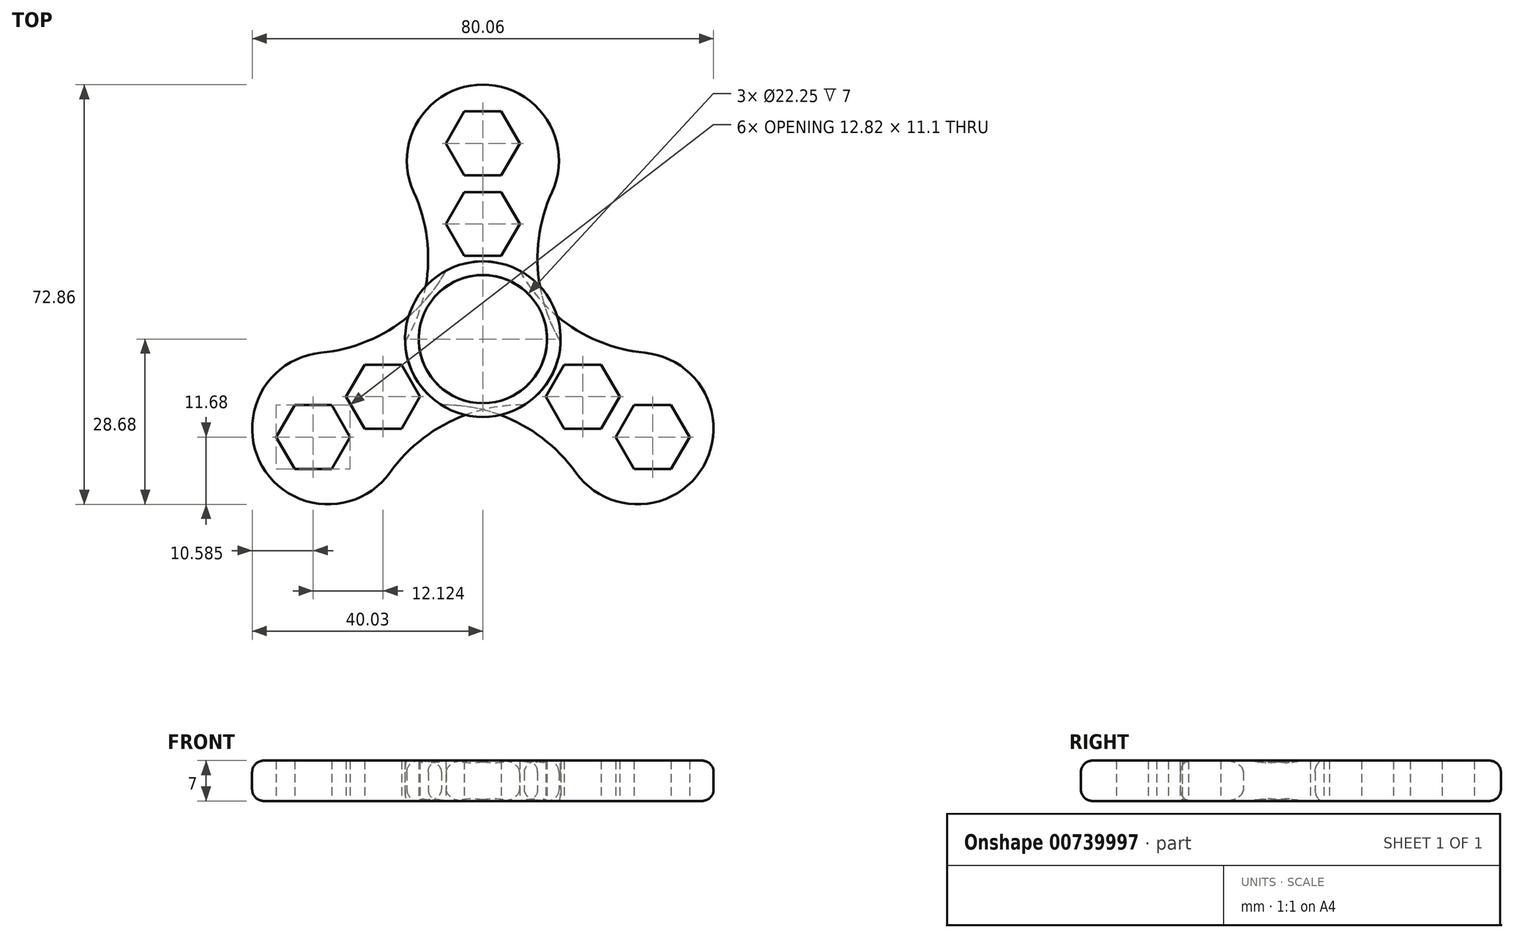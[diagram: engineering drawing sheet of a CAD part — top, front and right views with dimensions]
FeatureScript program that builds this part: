
annotation { "Feature Type Name" : "Feature", "Feature Type Description" : "" }
export const myFeature = defineFeature(function(context is Context, id is Id, definition is map)
    precondition{}
    {
        {
            var Q0;
            Q0=qCreatedBy(makeId("Top.planeOp"),FACE);
            var sketch = newSketch(context, id + "F0", { "sketchPlane" : qUnion([Q0])});
            skCircle(sketch, "E0", {"center": v(0, 0) * mm, "radius": 11.12 * mm});
            skCircle(sketch, "E1.cCircle", {"center": v(0, 20) * mm, "radius": 5.55 * mm, "construction": true});
            skLineSegment(sketch, "E1.0", {"start": v(3.2, 14.45) * mm, "end": v(-3.2, 14.45) * mm});
            skLineSegment(sketch, "E1.1", {"start": v(-3.2, 14.45) * mm, "end": v(-6.4, 20) * mm});
            skLineSegment(sketch, "E1.2", {"start": v(-6.4, 20) * mm, "end": v(-3.2, 25.55) * mm});
            skLineSegment(sketch, "E1.3", {"start": v(-3.2, 25.55) * mm, "end": v(3.2, 25.55) * mm});
            skLineSegment(sketch, "E1.4", {"start": v(3.2, 25.55) * mm, "end": v(6.4, 20) * mm});
            skLineSegment(sketch, "E1.5", {"start": v(6.4, 20) * mm, "end": v(3.2, 14.45) * mm});
            skPoint(sketch, "E1.0.midPoint", {"position": v(0, 14.45) * mm});
            skArc(sketch, "E2", {"start": v(-13.5, -0.48) * mm, "mid": v(0, -13.5) * mm, "end": v(13.5, -0.48) * mm});
            skArc(sketch, "E3", {"start": v(-6.64, 19.6) * mm, "mid": v(-6.05, 19.29) * mm, "end": v(-5.46, 19) * mm});
            skArc(sketch, "E4", {"start": v(-13.5, -0.48) * mm, "mid": v(-9.53, 12.35) * mm, "end": v(-12, 25.54) * mm});
            skArc(sketch, "E5", {"start": v(12, 25.54) * mm, "mid": v(9.53, 12.35) * mm, "end": v(13.5, -0.48) * mm});
            skPoint(sketch, "E6", {"position": v(0, 25.55) * mm});
            skCircle(sketch, "E7.cCircle", {"center": v(0, 34) * mm, "radius": 5.55 * mm, "construction": true});
            skLineSegment(sketch, "E7.0", {"start": v(3.2, 28.45) * mm, "end": v(-3.2, 28.45) * mm});
            skLineSegment(sketch, "E7.1", {"start": v(-3.2, 28.45) * mm, "end": v(-6.4, 34) * mm});
            skLineSegment(sketch, "E7.2", {"start": v(-6.4, 34) * mm, "end": v(-3.2, 39.55) * mm});
            skLineSegment(sketch, "E7.3", {"start": v(-3.2, 39.55) * mm, "end": v(3.2, 39.55) * mm});
            skLineSegment(sketch, "E7.4", {"start": v(3.2, 39.55) * mm, "end": v(6.4, 34) * mm});
            skLineSegment(sketch, "E7.5", {"start": v(6.4, 34) * mm, "end": v(3.2, 28.45) * mm});
            skPoint(sketch, "E7.0.midPoint", {"position": v(0, 28.45) * mm});
            skArc(sketch, "E8.trimOffspring", {"start": v(5.46, 19) * mm, "mid": v(6.05, 19.29) * mm, "end": v(6.64, 19.6) * mm});
            skArc(sketch, "E9.trimOffspring", {"start": v(12, 25.54) * mm, "mid": v(0, 44.18) * mm, "end": v(-12, 25.54) * mm});
            skSolve(sketch);
        }
        {
            var Q0;
            Q0=makeQuery(id+"F0.imprint","IMPRINT",FACE,{"disambiguationData":[TD([[makeQuery(id+"F0.imprint","IMPRINT",EDGE,{"derivedFrom":sQuery(id+"F0.wireOp",EDGE,"E0")}),-1.0]])]});
            extrude(context, id + "F1", {"entities" : qUnion([Q0]), "depth" : 7 * mm, "offsetDistance" : 25 * mm});
        }
        {
            var Q0;
            Q0=makeQuery(id+"F1.opExtrude","SWEPT_BODY",BODY,{"disambiguationData":[OSD([sQuery(id+"F0.wireOp",EDGE,"E0"),sQuery(id+"F0.wireOp",EDGE,"MDsEToRO-sDo8-RBbG-tWF8-SreFTiSiscwj"),sQuery(id+"F0.wireOp",EDGE,"8695b1e1-9288-4cb8-b92b-e351c22f4dc8.0"),sQuery(id+"F0.wireOp",EDGE,"8695b1e1-9288-4cb8-b92b-e351c22f4dc8.1"),sQuery(id+"F0.wireOp",EDGE,"8695b1e1-9288-4cb8-b92b-e351c22f4dc8.2"),sQuery(id+"F0.wireOp",EDGE,"8695b1e1-9288-4cb8-b92b-e351c22f4dc8.3"),sQuery(id+"F0.wireOp",EDGE,"8695b1e1-9288-4cb8-b92b-e351c22f4dc8.4"),sQuery(id+"F0.wireOp",EDGE,"8695b1e1-9288-4cb8-b92b-e351c22f4dc8.5"),sQuery(id+"F0.wireOp",EDGE,"7e2a876e-0c3f-4791-89cb-893942d8e054.0"),sQuery(id+"F0.wireOp",EDGE,"7e2a876e-0c3f-4791-89cb-893942d8e054.1"),sQuery(id+"F0.wireOp",EDGE,"7e2a876e-0c3f-4791-89cb-893942d8e054.2"),sQuery(id+"F0.wireOp",EDGE,"7e2a876e-0c3f-4791-89cb-893942d8e054.3"),sQuery(id+"F0.wireOp",EDGE,"7e2a876e-0c3f-4791-89cb-893942d8e054.4"),sQuery(id+"F0.wireOp",EDGE,"7e2a876e-0c3f-4791-89cb-893942d8e054.5"),sQuery(id+"F0.wireOp",EDGE,"6b78wPmF-SaVM-O4K7-W1F7-SZ1nQxVpJnyN"),sQuery(id+"F0.wireOp",EDGE,"JJtaek0i-86pv-hUof-ZRD0-zzxheRi3Trb6"),sQuery(id+"F0.wireOp",EDGE,"4f531992-08b8-4dfa-bfd4-d564cd5343f0.trimOffspring")])]});
            var Q1;
            Q1=makeQuery(id+"F1.opExtrude","CAP_EDGE",EDGE,{"disambiguationData":[OSD([sQuery(id+"F0.wireOp",EDGE,"E0")])],"isStart":false});
            circularPattern(context, id + "F2", {"entities" : qUnion([Q0]), "axis" : qUnion([Q1]), "angle" : 360 * degree, "instanceCount" : 3, "equalSpace" : true});
        }
        {
            var Q0;
            Q0=makeQuery(id+"F2.opPattern","COPY",EDGE,{"derivedFrom":makeQuery(id+"F1.opExtrude","CAP_EDGE",EDGE,{"disambiguationData":[OSD([sQuery(id+"F0.wireOp",EDGE,"E4")])],"isStart":false}),"instanceName":"2"});
            var Q1;
            Q1=makeQuery(id+"F2.opPattern","COPY",EDGE,{"derivedFrom":makeQuery(id+"F1.opExtrude","CAP_EDGE",EDGE,{"disambiguationData":[OSD([sQuery(id+"F0.wireOp",EDGE,"E9.trimOffspring")])],"isStart":true}),"instanceName":"2"});
            var Q2;
            Q2=makeQuery(id+"F2.opPattern","COPY",EDGE,{"derivedFrom":makeQuery(id+"F1.opExtrude","CAP_EDGE",EDGE,{"disambiguationData":[OSD([sQuery(id+"F0.wireOp",EDGE,"E9.trimOffspring")])],"isStart":true}),"instanceName":"1"});
            var Q3;
            Q3=makeQuery(id+"F2.opPattern","COPY",EDGE,{"derivedFrom":makeQuery(id+"F1.opExtrude","CAP_EDGE",EDGE,{"disambiguationData":[OSD([sQuery(id+"F0.wireOp",EDGE,"E9.trimOffspring")])],"isStart":false}),"instanceName":"1"});
            var Q4;
            Q4=makeQuery(id+"F2.opPattern","COPY",EDGE,{"derivedFrom":makeQuery(id+"F1.opExtrude","CAP_EDGE",EDGE,{"disambiguationData":[OSD([sQuery(id+"F0.wireOp",EDGE,"E4")])],"isStart":true}),"instanceName":"2"});
            var Q5;
            Q5=makeQuery(id+"F1.opExtrude","CAP_EDGE",EDGE,{"disambiguationData":[OSD([sQuery(id+"F0.wireOp",EDGE,"E5")])],"isStart":true});
            var Q6;
            Q6=makeQuery(id+"F1.opExtrude","CAP_EDGE",EDGE,{"disambiguationData":[OSD([sQuery(id+"F0.wireOp",EDGE,"E9.trimOffspring")])],"isStart":true});
            var Q7;
            Q7=makeQuery(id+"F1.opExtrude","CAP_EDGE",EDGE,{"disambiguationData":[OSD([sQuery(id+"F0.wireOp",EDGE,"E4")])],"isStart":true});
            var Q8;
            Q8=makeQuery(id+"F2.opPattern","COPY",EDGE,{"derivedFrom":makeQuery(id+"F1.opExtrude","CAP_EDGE",EDGE,{"disambiguationData":[OSD([sQuery(id+"F0.wireOp",EDGE,"E5")])],"isStart":true}),"instanceName":"1"});
            var Q9;
            Q9=makeQuery(id+"F2.opPattern","COPY",EDGE,{"derivedFrom":makeQuery(id+"F1.opExtrude","CAP_EDGE",EDGE,{"disambiguationData":[OSD([sQuery(id+"F0.wireOp",EDGE,"E4")])],"isStart":true}),"instanceName":"1"});
            var Q10;
            Q10=makeQuery(id+"F2.opPattern","COPY",EDGE,{"derivedFrom":makeQuery(id+"F1.opExtrude","CAP_EDGE",EDGE,{"disambiguationData":[OSD([sQuery(id+"F0.wireOp",EDGE,"E5")])],"isStart":true}),"instanceName":"2"});
            var Q11;
            Q11=makeQuery(id+"F2.opPattern","COPY",EDGE,{"derivedFrom":makeQuery(id+"F1.opExtrude","CAP_EDGE",EDGE,{"disambiguationData":[OSD([sQuery(id+"F0.wireOp",EDGE,"E9.trimOffspring")])],"isStart":false}),"instanceName":"2"});
            var Q12;
            Q12=makeQuery(id+"F2.opPattern","COPY",EDGE,{"derivedFrom":makeQuery(id+"F1.opExtrude","CAP_EDGE",EDGE,{"disambiguationData":[OSD([sQuery(id+"F0.wireOp",EDGE,"E4")])],"isStart":false}),"instanceName":"1"});
            var Q13;
            Q13=makeQuery(id+"F2.opPattern","COPY",EDGE,{"derivedFrom":makeQuery(id+"F1.opExtrude","CAP_EDGE",EDGE,{"disambiguationData":[OSD([sQuery(id+"F0.wireOp",EDGE,"E5")])],"isStart":false}),"instanceName":"1"});
            var Q14;
            Q14=makeQuery(id+"F1.opExtrude","CAP_EDGE",EDGE,{"disambiguationData":[OSD([sQuery(id+"F0.wireOp",EDGE,"E4")])],"isStart":false});
            var Q15;
            Q15=makeQuery(id+"F1.opExtrude","CAP_EDGE",EDGE,{"disambiguationData":[OSD([sQuery(id+"F0.wireOp",EDGE,"E9.trimOffspring")])],"isStart":false});
            var Q16;
            Q16=makeQuery(id+"F2.opPattern","COPY",EDGE,{"derivedFrom":makeQuery(id+"F1.opExtrude","CAP_EDGE",EDGE,{"disambiguationData":[OSD([sQuery(id+"F0.wireOp",EDGE,"E5")])],"isStart":false}),"instanceName":"2"});
            fillet(context, id + "F3", {"entities" : qUnion([Q0, Q1, Q2, Q3, Q4, Q5, Q6, Q7, Q8, Q9, Q10, Q11, Q12, Q13, Q14, Q15, Q16]), "radius" : 2 * mm, "tangentPropagation" : true, "allowEdgeOverflow" : false});
        }
    });
